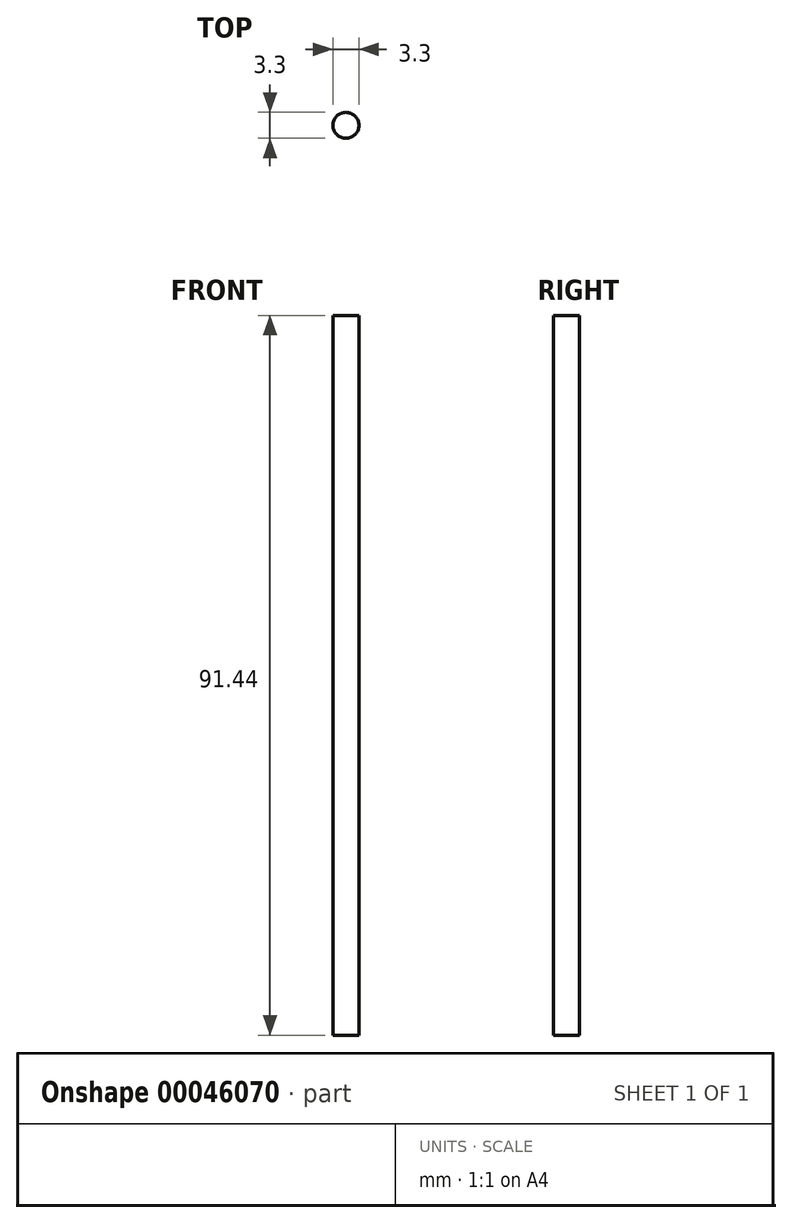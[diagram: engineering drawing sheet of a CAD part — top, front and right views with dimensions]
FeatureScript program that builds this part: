
annotation { "Feature Type Name" : "Feature", "Feature Type Description" : "" }
export const myFeature = defineFeature(function(context is Context, id is Id, definition is map)
    precondition{}
    {
        {
            var Q0;
            Q0=qCreatedBy(makeId("Top.planeOp"),FACE);
            var sketch = newSketch(context, id + "F0", { "sketchPlane" : qUnion([Q0])});
            skCircle(sketch, "E0", {"center": v(0, 0) * mm, "radius": 1.65 * mm});
            skLineSegment(sketch, "E1", {"start": v(0, 0) * mm, "end": v(0, 1.65) * mm});
            skSolve(sketch);
        }
        {
            var Q0;
            Q0=makeQuery(id+"F0.imprint","IMPRINT",FACE,{"disambiguationData":[TD([[makeQuery(id+"F0.imprint","IMPRINT",EDGE,{"derivedFrom":sQuery(id+"F0.wireOp",EDGE,"E0")}),1.0]])]});
            extrude(context, id + "F1", {"entities" : qUnion([Q0]), "depth" : 91.44 * mm});
        }
    });
